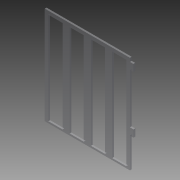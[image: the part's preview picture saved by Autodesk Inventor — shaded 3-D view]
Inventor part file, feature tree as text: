
AUTODESK INVENTOR PART (.ipt)
format: ipt  version: 2013 (Build 170138000, 138)  size: 135,168 bytes
history: native  units: in
note: dims shown in document units (in); Inventor stores cm internally (conversion verified against a paired STEP export)
features: extrude x4, sketch x4
ambient origin geometry x8: Origin, YZ Plane, XZ Plane, XY Plane, X Axis, Y Axis, Z Axis, Center Point
bodies: Solid1 (feature_tree)
feature tree (8):
  extrude  "Extrusion1"  Depth=6.0in
  extrude  "Extrusion2"  Depth=0.25in
  extrude  "Extrusion3"  Depth=0.25in
  extrude  "Extrusion4"  Depth=3.5in
  sketch  "Sketch1"  dims[d0=7.0in d1=6.0in]
  sketch  "Sketch2"  dims[d7=0.125in d8=0.0in d9=0.25in]
  sketch  "Sketch3"  dims[d10=0.5in d11=0.25in]
  sketch  "Sketch4"  dims[d12=0.5in d13=3.5in d14=0.25in d15=0.125in d16=0.0in d17=1.0in d18=1.0in d20=0.25in d21=0.25in d22=0.25in d23=1.5748in d25=1.5in d26=0.3937in d28=1.0in d30=0.125in d31=0.0in d32=0.15in d33=1.0in d34=0.0in]
